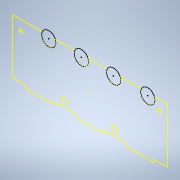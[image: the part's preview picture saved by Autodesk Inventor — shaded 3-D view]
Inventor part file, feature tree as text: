
AUTODESK INVENTOR PART (.ipt)
format: ipt  version: 2022 (Build 260153000, 153)  size: 97,280 bytes
history: native  units: mm
features: other x2, sketch x1, reference x1
ambient origin geometry x8: Origin, YZ Plane, XZ Plane, XY Plane, X Axis, Y Axis, Z Axis, Center Point
feature tree (4):
  sketch  "Sketch1"
  reference  "Reference1"
  other  "Caja_Reductora_.iam"
  other  "Carcasa_CajaR_Lateral1:1"
